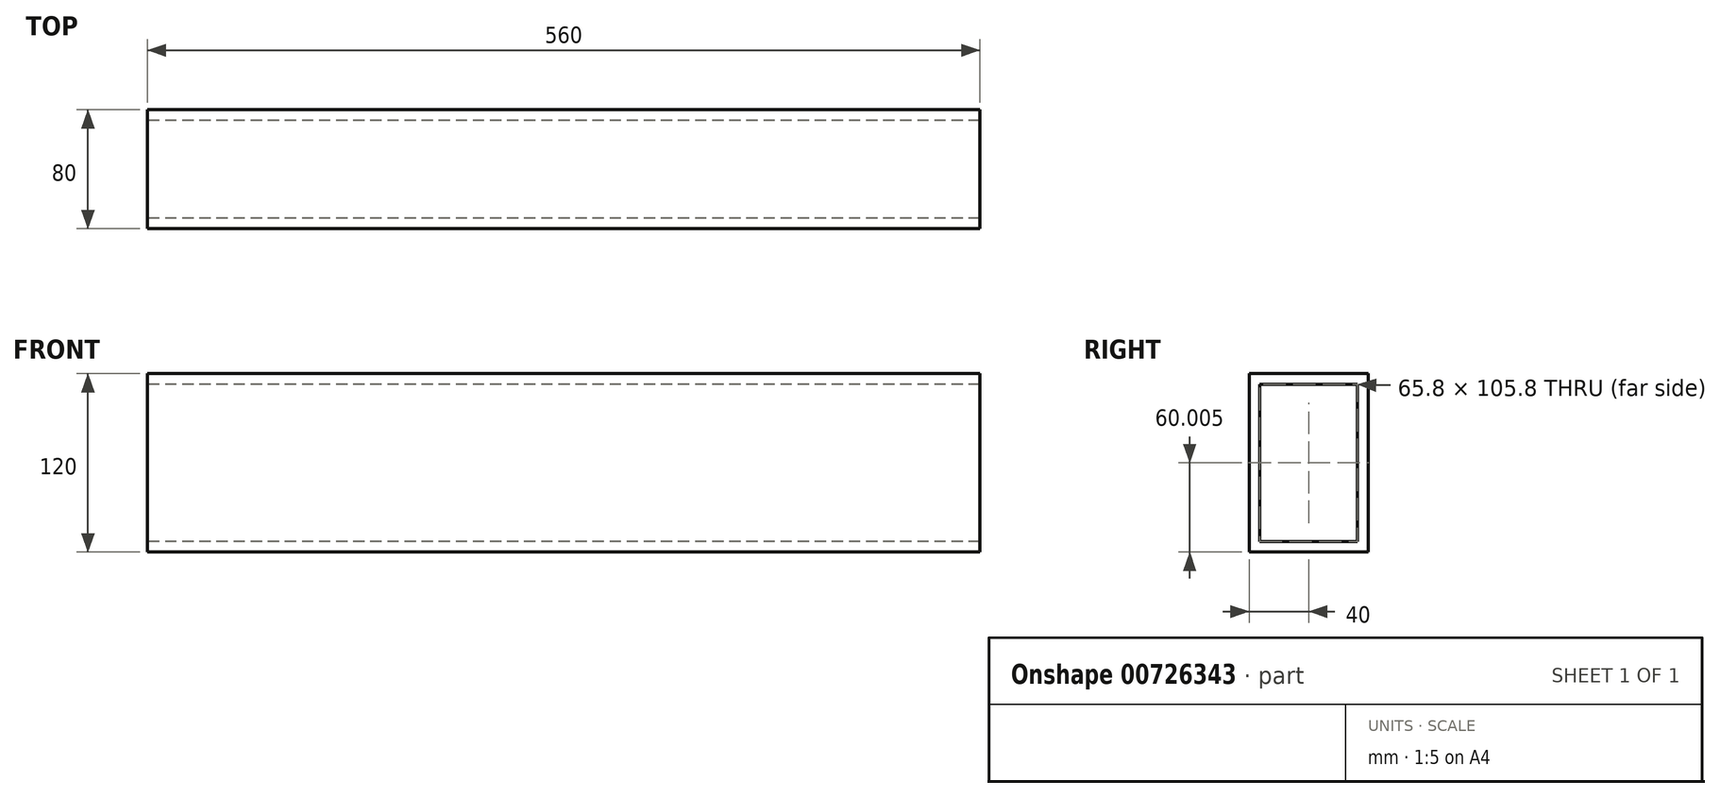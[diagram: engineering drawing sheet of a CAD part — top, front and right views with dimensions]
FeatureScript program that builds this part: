
annotation { "Feature Type Name" : "Feature", "Feature Type Description" : "" }
export const myFeature = defineFeature(function(context is Context, id is Id, definition is map)
    precondition{}
    {
        {
            var Q0;
            Q0=qCreatedBy(makeId("Front.planeOp"),FACE);
            var sketch = newSketch(context, id + "F0", { "sketchPlane" : qUnion([Q0])});
            skLineSegment(sketch, "E0.bottom", {"start": v(-277.57, -154.82) * mm, "end": v(282.43, -154.82) * mm});
            skLineSegment(sketch, "E0.top", {"start": v(-277.57, -34.82) * mm, "end": v(282.43, -34.82) * mm});
            skLineSegment(sketch, "E0.left", {"start": v(-277.57, -154.82) * mm, "end": v(-277.57, -34.82) * mm});
            skLineSegment(sketch, "E0.right", {"start": v(282.43, -154.82) * mm, "end": v(282.43, -34.82) * mm});
            skSolve(sketch);
        }
        {
            var Q0;
            Q0 = qSketchRegion(id + "F0", true);
            extrude(context, id + "F1", {"entities" : qUnion([Q0]), "depth" : 80 * mm, "offsetDistance" : 25 * mm});
        }
        {
            var Q0;
            Q0=makeQuery(id+"F1.opExtrude","SWEPT_FACE",FACE,{"disambiguationData":[OSD([sQuery(id+"F0.wireOp",EDGE,"E0.left")])]});
            var sketch = newSketch(context, id + "F2", { "sketchPlane" : qUnion([Q0])});
            skLineSegment(sketch, "E1.bottom", {"start": v(7.1, -41.92) * mm, "end": v(72.9, -41.92) * mm});
            skLineSegment(sketch, "E1.top", {"start": v(7.1, -147.72) * mm, "end": v(72.9, -147.72) * mm});
            skLineSegment(sketch, "E1.left", {"start": v(7.1, -41.92) * mm, "end": v(7.1, -147.72) * mm});
            skLineSegment(sketch, "E1.right", {"start": v(72.9, -41.92) * mm, "end": v(72.9, -147.72) * mm});
            skSolve(sketch);
        }
        {
            var Q0;
            Q0=makeQuery(id+"F2.imprint","IMPRINT",FACE,{"disambiguationData":[TD([[makeQuery(id+"F2.imprint","IMPRINT",EDGE,{"derivedFrom":sQuery(id+"F2.wireOp",EDGE,"E1.bottom")}),-1.0]])]});
            extrude(context, id + "F3", {"entities" : qUnion([Q0]), "operationType" : NewBodyOperationType.REMOVE, "oppositeDirection" : true, "depth" : 560 * mm, "offsetDistance" : 25 * mm});
        }
    });
